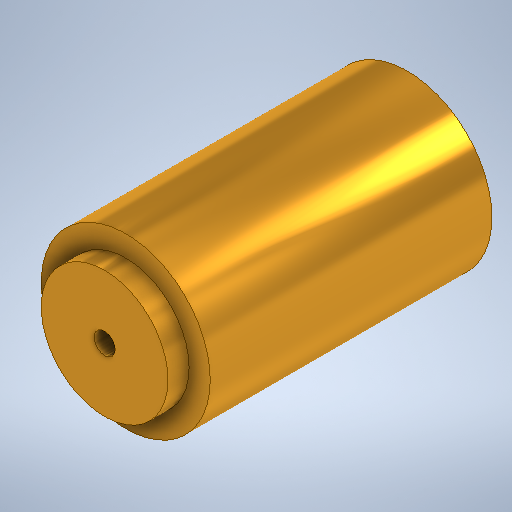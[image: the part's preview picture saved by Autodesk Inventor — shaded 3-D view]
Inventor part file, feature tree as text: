
AUTODESK INVENTOR PART (.ipt)
format: ipt  version: 2025.1 (Build 291241000, 241)  size: 273,408 bytes
history: native  units: mm
features: sketch x3, hole x2, revolve x1
ambient origin geometry x8: Origin, YZ Plane, XZ Plane, XY Plane, X Axis, Y Axis, Z Axis, Center Point
bodies: Volumenkörper1 (feature_tree)
feature tree (6):
  revolve  "Umdrehung1"
  hole  "Bohrung1"  [1 undecoded]
  hole  "Hole2"  [1 undecoded]
  sketch  "Skizze2"  dims[d1=21.5mm d2=1.5mm]
  sketch  "Skizze3"  dims[d3=12.0mm d4=9.0mm]
  sketch  "Sketch4"  dims[d5=90.0deg d6=8.0mm d7=6.0mm d8=4.0mm d9=2.0mm d10=90.0deg d11=18.0mm d12=0.0mm d13=1.5mm d14=5.0mm d15=4.0mm d16=2.0mm d17=90.0deg d18=5.0mm d19=0.0mm]
note: 2 required parameter values undecoded (feature->parameter linkage not recoverable at this tier; creation-order binding heuristic only, values carry confidence <= 0.55)
